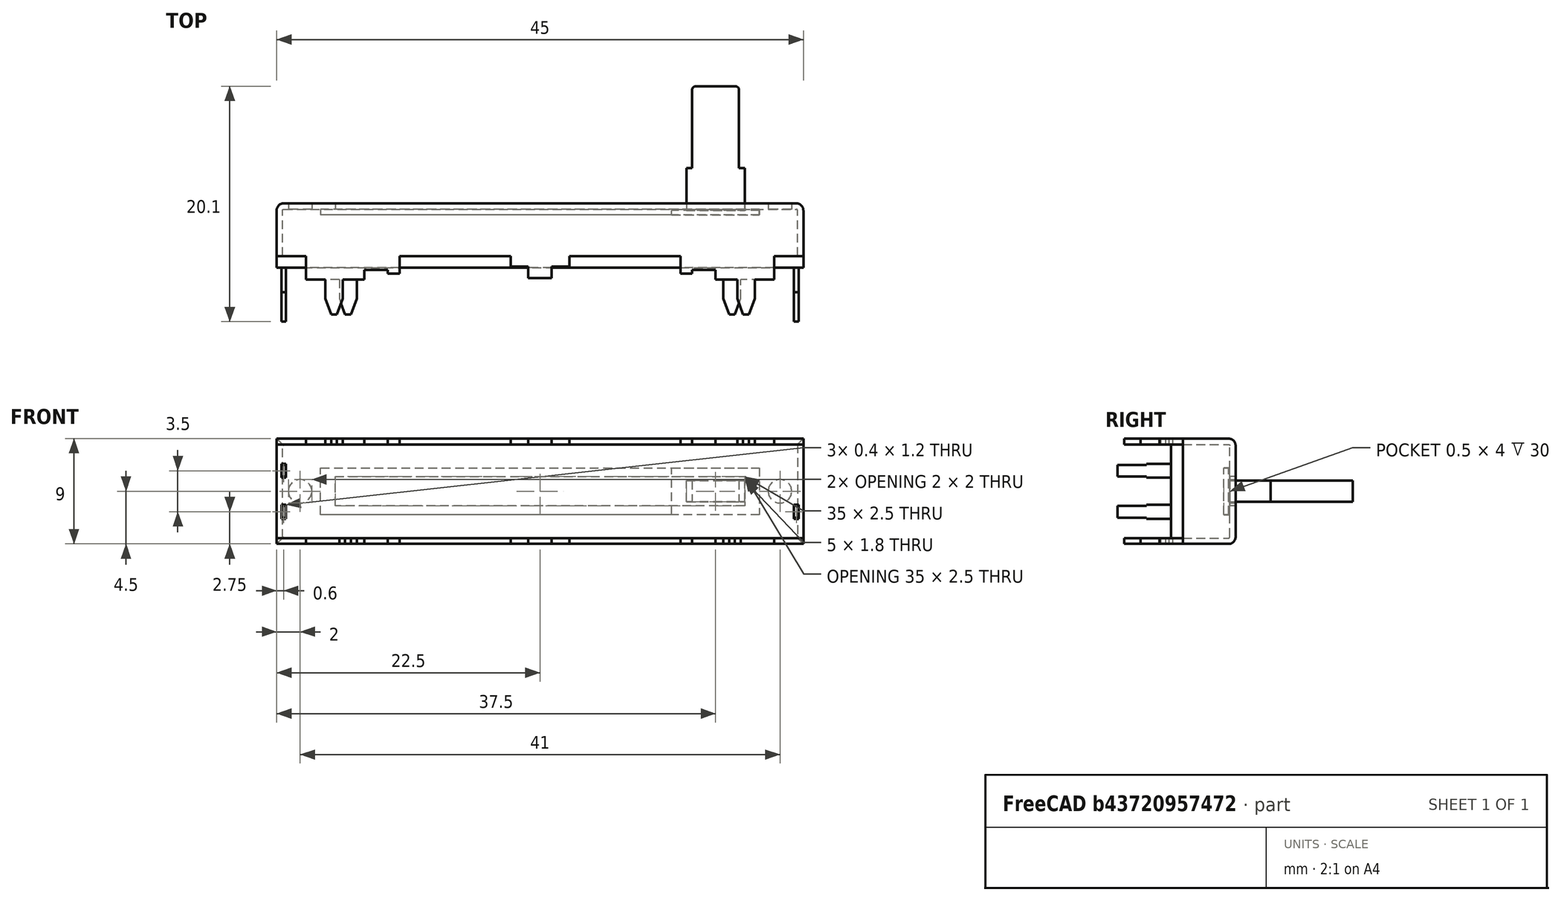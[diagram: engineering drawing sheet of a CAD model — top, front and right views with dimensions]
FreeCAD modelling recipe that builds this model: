
FCSTD DOCUMENT  (FreeCAD 1.0R38641 +468 (Git))
Label: THT-FADER
License: All rights reserved
LicenseURL: https://en.wikipedia.org/wiki/All_rights_reserved
objects: Part::Feature×3, PartDesign::Boolean×1, PartDesign::Body×1
note: 6 computed .brp shape members not serialized (recipe doc carries the construction recipe); baked Part::Feature solids carry a one-line shape summary decoded from their .brp

FEATURE [Part::Feature] Part__Feature001  label="BM-519-4"
  Placement = pos=(0,1,0) rot=(0,0,1;0rad)
  shape: bbox 45 x 9.6 x 8 mm, 46 faces (baked)
FEATURE [Part::Feature] Part__Feature002  label="BM-679"
  Placement = pos=(15,5.5,0) rot=(0,0,1;0rad)
  shape: bbox 7.5 x 11 x 4 mm, 17 faces (baked)
FEATURE [Part::Feature] Part__Feature  label="BM-517-4"
  shape: bbox 45 x 9.5 x 9 mm, 98 faces (baked)
FEATURE [PartDesign::Boolean] Boolean
  Group = -> [Part__Feature001,Part__Feature,Part__Feature002]
  Suppressed = false
  Type = 0
  UsePlacement = false
FEATURE [PartDesign::Body] Body  label="THT-FADER"
  AllowCompound = false
  Group = -> [Boolean]
  Origin = -> Origin
  Tip = -> Boolean
